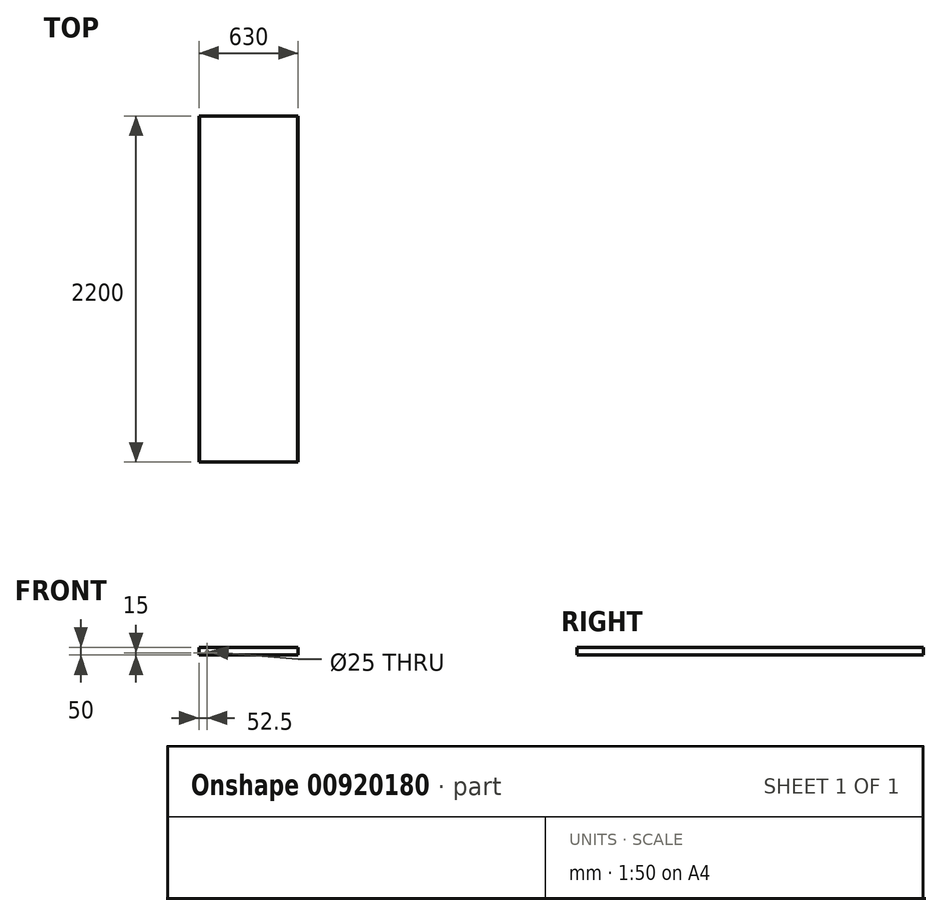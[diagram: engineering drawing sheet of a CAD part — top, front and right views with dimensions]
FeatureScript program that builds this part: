
annotation { "Feature Type Name" : "Feature", "Feature Type Description" : "" }
export const myFeature = defineFeature(function(context is Context, id is Id, definition is map)
    precondition{}
    {
        {
            var Q0;
            Q0=qCreatedBy(makeId("Front.planeOp"),FACE);
            var sketch = newSketch(context, id + "F0", { "sketchPlane" : qUnion([Q0])});
            skLineSegment(sketch, "E0.bottom", {"start": v(0, 0) * mm, "end": v(630, 0) * mm});
            skLineSegment(sketch, "E0.top", {"start": v(0, 50) * mm, "end": v(630, 50) * mm});
            skLineSegment(sketch, "E0.left", {"start": v(0, 0) * mm, "end": v(0, 50) * mm});
            skLineSegment(sketch, "E0.right", {"start": v(630, 0) * mm, "end": v(630, 50) * mm});
            skSolve(sketch);
        }
        {
            var Q0;
            Q0 = qSketchRegion(id + "F0", true);
            extrude(context, id + "F1", {"entities" : qUnion([Q0]), "depth" : 2200 * mm, "offsetDistance" : 25 * mm});
        }
        {
            var Q0;
            Q0=makeQuery(id+"F1.opExtrude","SWEPT_FACE",FACE,{"disambiguationData":[OSD([sQuery(id+"F0.wireOp",EDGE,"E0.top")])]});
            shell(context, id + "F2", {"entities" : qUnion([Q0]), "thickness" : 2.5 * mm});
        }
        {
            var Q0;
            {var subQ0=sQuery(id+"F0.wireOp",EDGE,"E0.right");var subQ1=sQuery(id+"F0.wireOp",EDGE,"E0.left");var subQ2=sQuery(id+"F0.wireOp",EDGE,"E0.top");var subQ3=sQuery(id+"F0.wireOp",EDGE,"E0.bottom");Q0=makeQuery(id+"F2.opShell","OFFSET_FACE",FACE,{"disambiguationData":[OSD([subQ3,subQ2,subQ1,subQ0]),TDD([makeQuery(id+"F1.opExtrude","CAP_FACE",FACE,{"disambiguationData":[OSD([subQ3,subQ2,subQ1,subQ0])],"isStart":true})])]});}
            var sketch = newSketch(context, id + "F3", { "sketchPlane" : qUnion([Q0])});
            skLineSegment(sketch, "E1", {"start": v(2.5, 2.5) * mm, "end": v(52.5, 2.5) * mm});
            skLineSegment(sketch, "E2", {"start": v(52.5, 2.5) * mm, "end": v(52.5, 15) * mm});
            skCircle(sketch, "E3", {"center": v(52.5, 15) * mm, "radius": 12.5 * mm});
            skSolve(sketch);
        }
        {
            var Q0;
            Q0=makeQuery(id+"F3.imprint","IMPRINT",FACE,{"disambiguationData":[TD([[makeQuery(id+"F3.imprint","IMPRINT",EDGE,{"derivedFrom":sQuery(id+"F3.wireOp",EDGE,"E3")}),1.0]])]});
            extrude(context, id + "F4", {"entities" : qUnion([Q0]), "operationType" : NewBodyOperationType.REMOVE, "oppositeDirection" : true, "depth" : 30 * mm, "offsetDistance" : 25 * mm});
        }
    });
